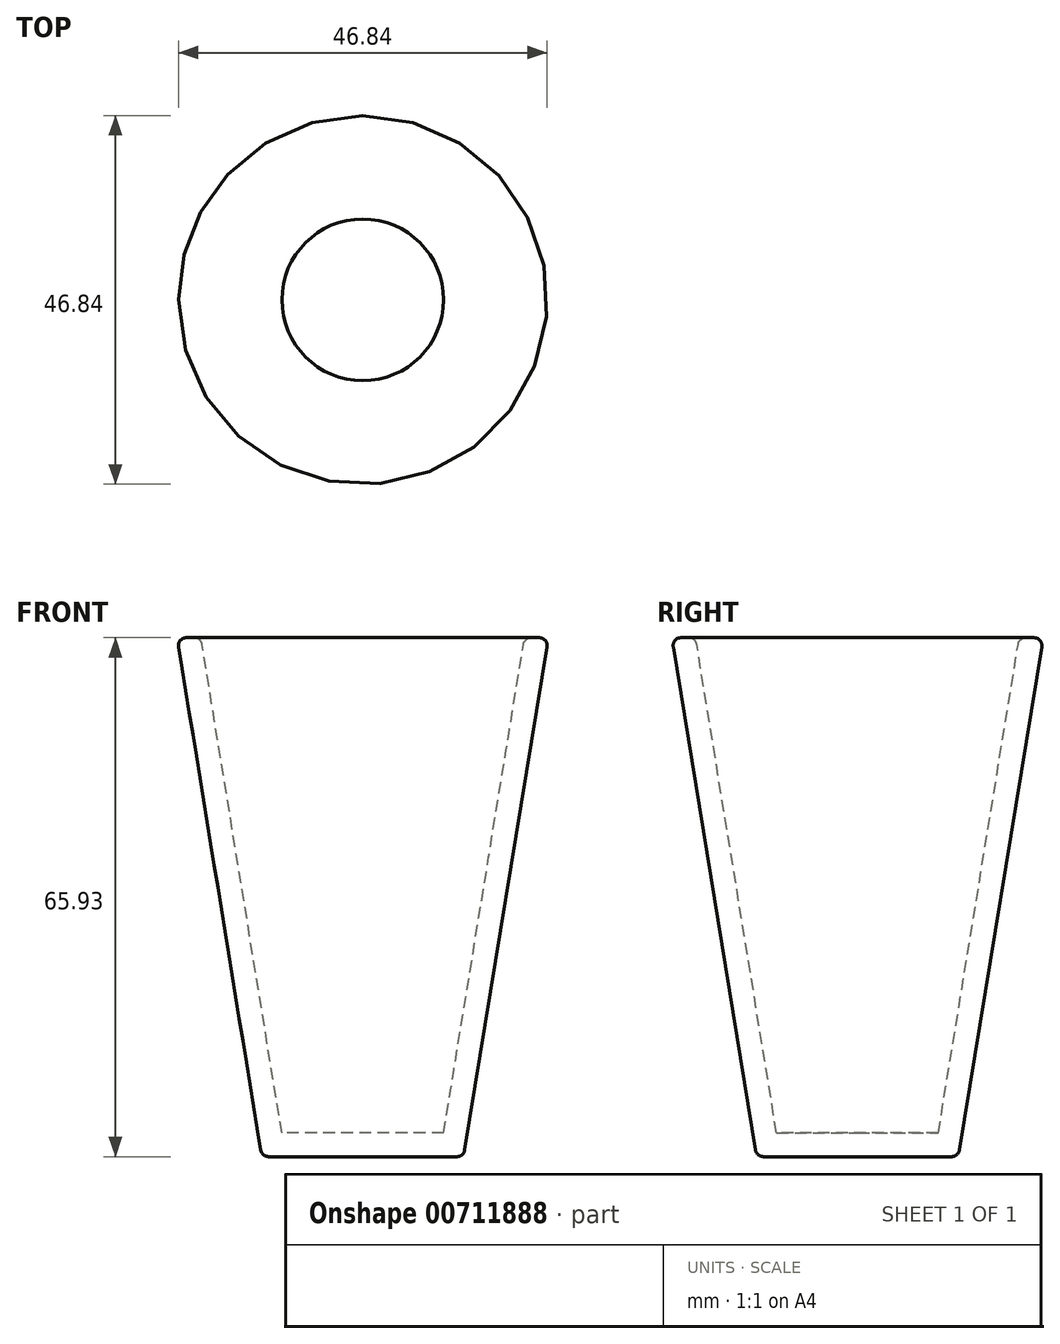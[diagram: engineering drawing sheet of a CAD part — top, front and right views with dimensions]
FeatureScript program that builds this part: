
annotation { "Feature Type Name" : "Feature", "Feature Type Description" : "" }
export const myFeature = defineFeature(function(context is Context, id is Id, definition is map)
    precondition{}
    {
        {
            var Q0;
            Q0=qCreatedBy(makeId("Front.planeOp"),FACE);
            var sketch = newSketch(context, id + "F0", { "sketchPlane" : qUnion([Q0])});
            skLineSegment(sketch, "E0", {"start": v(0, 0) * mm, "end": v(0, 65.93) * mm});
            skLineSegment(sketch, "E1", {"start": v(0, 65.93) * mm, "end": v(-23.6, 65.93) * mm});
            skLineSegment(sketch, "E2", {"start": v(-23.6, 65.93) * mm, "end": v(-12.82, 0) * mm});
            skLineSegment(sketch, "E3", {"start": v(-12.82, 0) * mm, "end": v(0, 0) * mm});
            skSolve(sketch);
        }
        {
            var Q0;
            Q0=makeQuery(id+"F0.imprint","IMPRINT",FACE,{"disambiguationData":[TD([[makeQuery(id+"F0.imprint","IMPRINT",EDGE,{"derivedFrom":sQuery(id+"F0.wireOp",EDGE,"E0")}),1.0]])]});
            var Q1;
            Q1=sQuery(id+"F0.wireOp",EDGE,"E0");
            revolve(context, id + "F1", {"surfaceOperationType" : NewSurfaceOperationType.NEW, "entities" : qUnion([Q0]), "axis" : qUnion([Q1]), "revolveType" : RevolveType.FULL});
        }
        {
            var Q0;
            Q0=makeQuery(id+"F1.opRevolve","SWEPT_FACE",FACE,{"disambiguationData":[OSD([sQuery(id+"F0.wireOp",EDGE,"E1")])]});
            shell(context, id + "F2", {"entities" : qUnion([Q0]), "thickness" : 3 * mm});
        }
        {
            var Q0;
            Q0=makeQuery(id+"F1.opRevolve","SWEPT_EDGE",EDGE,{"disambiguationData":[OSD([sQuery(id+"F0.wireOp",EDGE,"E1"),sQuery(id+"F0.wireOp",EDGE,"E2")])]});
            var Q1;
            Q1=makeQuery(id+"F2.opShell","OFFSET_EDGE",EDGE,{"disambiguationData":[OSD([sQuery(id+"F0.wireOp",EDGE,"E1"),sQuery(id+"F0.wireOp",EDGE,"E2")])]});
            var Q2;
            Q2=makeQuery(id+"F1.opRevolve","SWEPT_EDGE",EDGE,{"disambiguationData":[OSD([sQuery(id+"F0.wireOp",EDGE,"E2"),sQuery(id+"F0.wireOp",EDGE,"E3")])]});
            fillet(context, id + "F3", {"entities" : qUnion([Q0, Q1, Q2]), "radius" : 1 * mm, "tangentPropagation" : true, "allowEdgeOverflow" : false});
        }
    });
